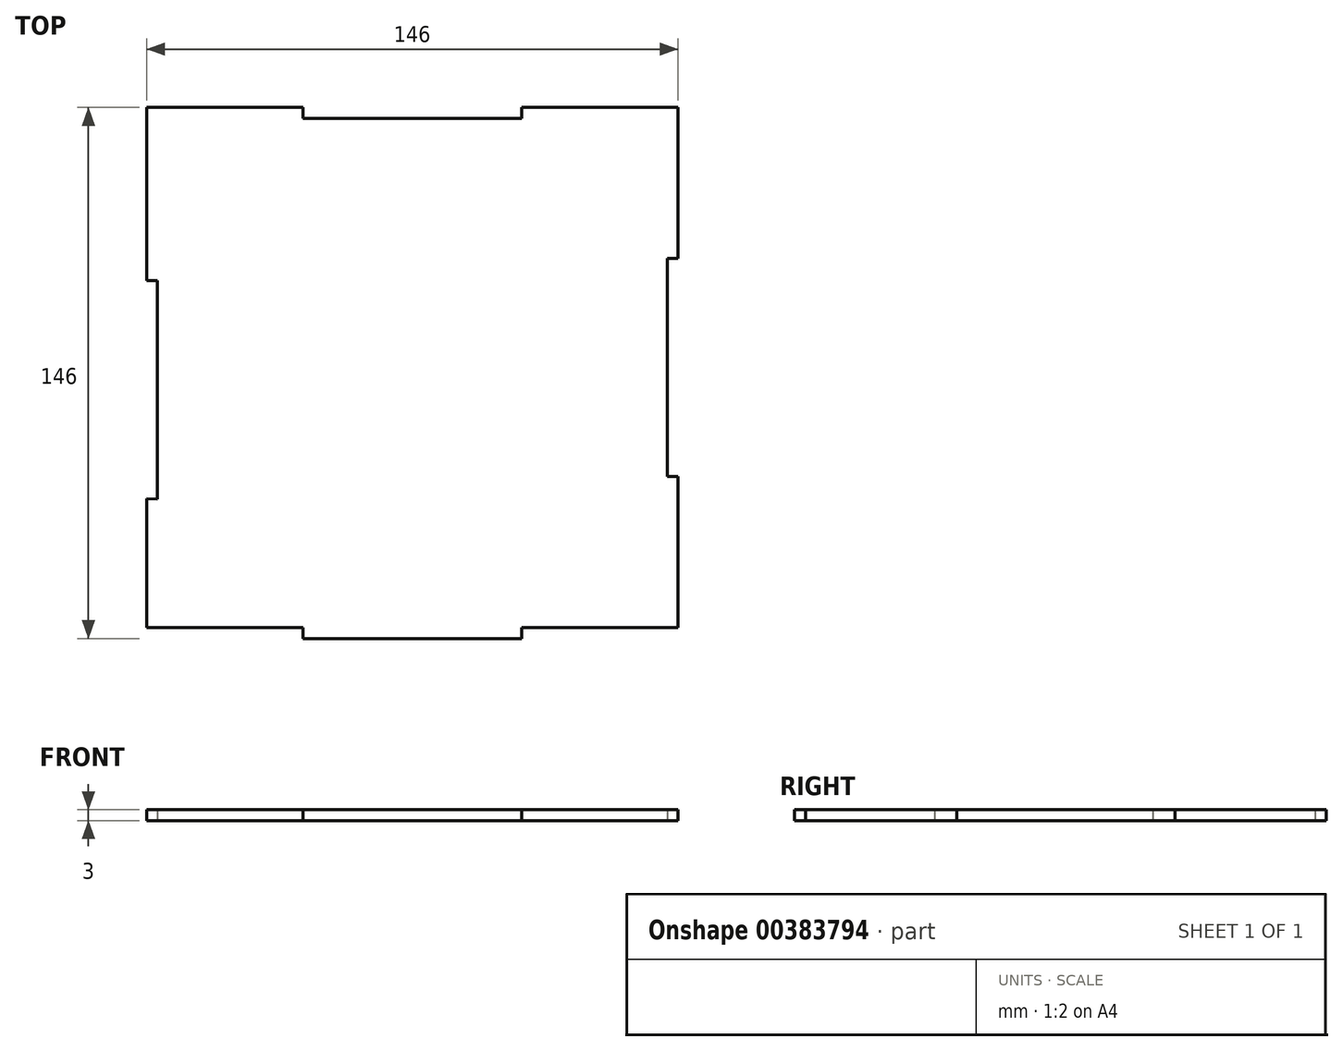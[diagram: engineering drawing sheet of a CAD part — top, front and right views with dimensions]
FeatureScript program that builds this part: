
annotation { "Feature Type Name" : "Feature", "Feature Type Description" : "" }
export const myFeature = defineFeature(function(context is Context, id is Id, definition is map)
    precondition{}
    {
        {
            var Q0;
            Q0=qCreatedBy(makeId("Top.planeOp"),FACE);
            var sketch = newSketch(context, id + "F0", { "sketchPlane" : qUnion([Q0])});
            skLineSegment(sketch, "E0.bottom", {"start": v(73, -71.5) * mm, "end": v(30, -71.5) * mm});
            skLineSegment(sketch, "E0.top", {"start": v(73, 71.5) * mm, "end": v(30, 71.5) * mm});
            skLineSegment(sketch, "E0.left", {"start": v(73, -71.5) * mm, "end": v(73, -30) * mm});
            skLineSegment(sketch, "E0.right", {"start": v(-73, -71.5) * mm, "end": v(-73, -36.07) * mm});
            skPoint(sketch, "E0.middle", {"position": v(0, 0) * mm});
            skLineSegment(sketch, "E1.bottom", {"start": v(30, -74.5) * mm, "end": v(-30, -74.5) * mm});
            skLineSegment(sketch, "E1.left", {"start": v(30, -74.5) * mm, "end": v(30, -71.5) * mm});
            skLineSegment(sketch, "E1.right", {"start": v(-30, -74.5) * mm, "end": v(-30, -71.5) * mm});
            skPoint(sketch, "E1.middle", {"position": v(0, -71.5) * mm});
            skPoint(sketch, "E2.orphan", {"position": v(-30, -68.5) * mm});
            skPoint(sketch, "E3.orphan", {"position": v(30, -68.5) * mm});
            skLineSegment(sketch, "E4.trimOffspring", {"start": v(-30, -71.5) * mm, "end": v(-73, -71.5) * mm});
            skLineSegment(sketch, "E5.bottom", {"start": v(30, 68.5) * mm, "end": v(-30, 68.5) * mm});
            skLineSegment(sketch, "E5.left", {"start": v(30, 68.5) * mm, "end": v(30, 71.5) * mm});
            skLineSegment(sketch, "E5.right", {"start": v(-30, 68.5) * mm, "end": v(-30, 71.5) * mm});
            skPoint(sketch, "E5.middle", {"position": v(0, 71.5) * mm});
            skPoint(sketch, "E6.orphan", {"position": v(-30, 74.5) * mm});
            skLineSegment(sketch, "E7.trimOffspring", {"start": v(-30, 71.5) * mm, "end": v(-73, 71.5) * mm});
            skPoint(sketch, "E8.orphan", {"position": v(30, 74.5) * mm});
            skPoint(sketch, "E9.middle", {"position": v(-73, 0) * mm});
            skLineSegment(sketch, "E10.trimOffspring", {"start": v(-73, 23.88) * mm, "end": v(-73, 71.5) * mm});
            skPoint(sketch, "E9.left.end.orphan", {"position": v(-70, 23.88) * mm});
            skPoint(sketch, "E9.left.start.orphan", {"position": v(-70, -36.12) * mm});
            skPoint(sketch, "E11.middle", {"position": v(73, 0) * mm});
            skPoint(sketch, "E11.right.end.orphan", {"position": v(70, 23.88) * mm});
            skLineSegment(sketch, "E12.trimOffspring", {"start": v(73, 30) * mm, "end": v(73, 71.5) * mm});
            skLineSegment(sketch, "E13", {"start": v(-73, -36.07) * mm, "end": v(-70, -36.12) * mm});
            skLineSegment(sketch, "E14", {"start": v(-73, 23.88) * mm, "end": v(-70, 23.88) * mm});
            skPoint(sketch, "E9.bottom.end.orphan", {"position": v(-76, -23.88) * mm});
            skPoint(sketch, "E9.top.end.orphan", {"position": v(-76, 36.12) * mm});
            skPoint(sketch, "E11.top.start.orphan", {"position": v(76, 36.12) * mm});
            skPoint(sketch, "E11.bottom.start.orphan", {"position": v(76, -23.88) * mm});
            skLineSegment(sketch, "E15", {"start": v(73, -30) * mm, "end": v(70, -30) * mm});
            skLineSegment(sketch, "E16", {"start": v(73, 30) * mm, "end": v(70, 30) * mm});
            skLineSegment(sketch, "E17", {"start": v(-70, 23.88) * mm, "end": v(-70, -36.12) * mm});
            skLineSegment(sketch, "E18", {"start": v(70, -30) * mm, "end": v(70, 30) * mm});
            skSolve(sketch);
        }
        {
            var Q0;
            Q0=qSketchRegion(id+"F0",true);
            extrude(context, id + "F1", {"entities" : qUnion([Q0]), "depth" : 3 * mm});
        }
    });
